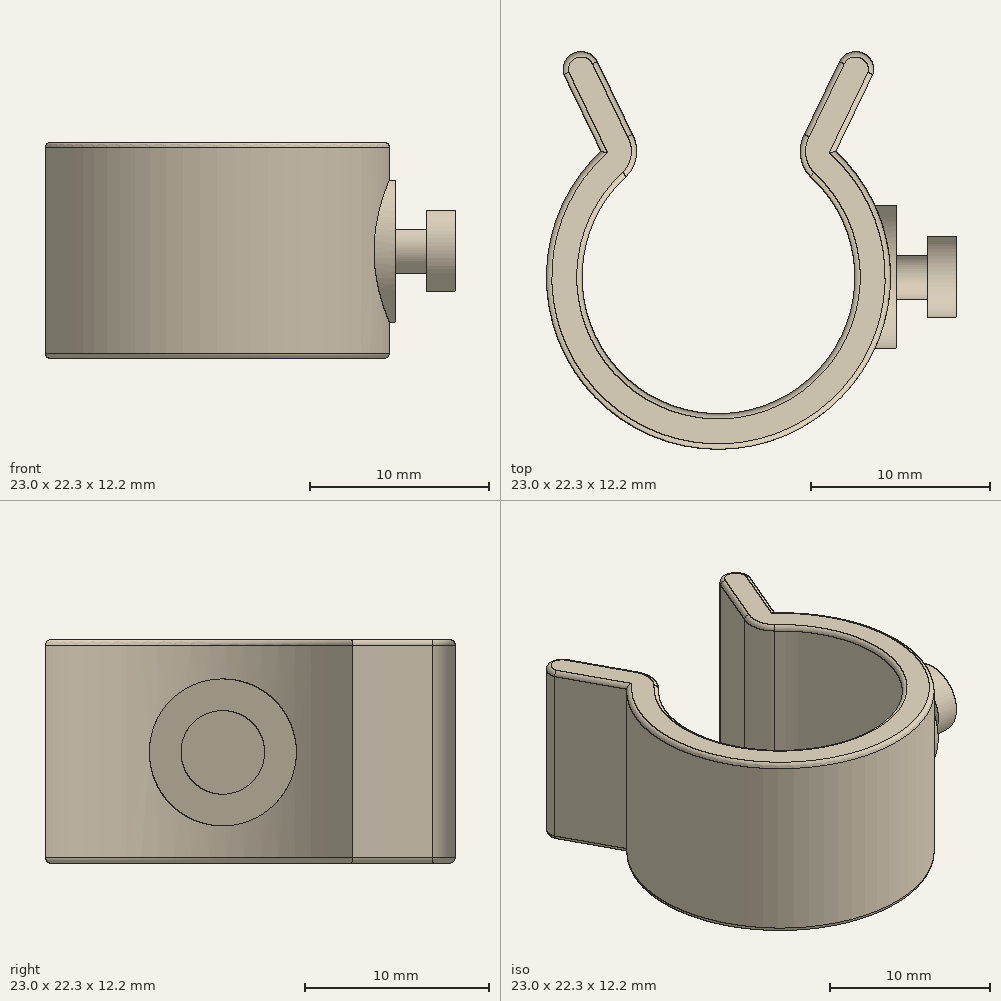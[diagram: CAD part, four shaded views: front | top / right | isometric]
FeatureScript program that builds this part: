
annotation { "Feature Type Name" : "Feature", "Feature Type Description" : "" }
export const myFeature = defineFeature(function(context is Context, id is Id, definition is map)
    precondition{}
    {
        {
            var Q0;
            Q0=qCreatedBy(makeId("Top.planeOp"),FACE);
            var sketch = newSketch(context, id + "F0", { "sketchPlane" : qUnion([Q0])});
            skArc(sketch, "E0", {"start": v(-5.16, 5.65) * mm, "mid": v(0, -7.65) * mm, "end": v(5.16, 5.65) * mm});
            skArc(sketch, "E1", {"start": v(-6.59, 7.05) * mm, "mid": v(0.01, -9.65) * mm, "end": v(6.57, 7.07) * mm});
            skLineSegment(sketch, "E2", {"start": v(7.65, 0) * mm, "end": v(9.65, 0) * mm, "construction": true});
            skArc(sketch, "E3", {"start": v(-5.16, 5.65) * mm, "mid": v(-4.6, 6.77) * mm, "end": v(-4.83, 8) * mm});
            skLineSegment(sketch, "E4", {"start": v(-6.59, 7.05) * mm, "end": v(-8.67, 11.38) * mm});
            skLineSegment(sketch, "E5", {"start": v(-4.83, 8) * mm, "end": v(-6.8, 12.09) * mm});
            skLineSegment(sketch, "E6.MirrorCS", {"start": v(4.83, 8) * mm, "end": v(6.8, 12.09) * mm});
            skLineSegment(sketch, "E7.MirrorCS", {"start": v(6.59, 7.05) * mm, "end": v(8.67, 11.38) * mm});
            skArc(sketch, "E8.MirrorCS", {"start": v(5.16, 5.65) * mm, "mid": v(4.6, 6.77) * mm, "end": v(4.83, 8) * mm});
            skLineSegment(sketch, "E9", {"start": v(-7.7, 11.65) * mm, "end": v(7.7, 11.65) * mm, "construction": true});
            skArc(sketch, "E10", {"start": v(-6.8, 12.09) * mm, "mid": v(-8.06, 12.6) * mm, "end": v(-8.67, 11.38) * mm});
            skArc(sketch, "E11.MirrorCS", {"start": v(6.8, 12.09) * mm, "mid": v(8.06, 12.6) * mm, "end": v(8.67, 11.38) * mm});
            skLineSegment(sketch, "E12", {"start": v(-4.6, 6.8) * mm, "end": v(4.6, 6.8) * mm, "construction": true});
            skSolve(sketch);
        }
        {
            var Q0;
            Q0 = qSketchRegion(id + "F0", true);
            extrude(context, id + "F1", {"entities" : qUnion([Q0]), "depth" : 12.15 * mm});
        }
        {
            var Q0;
            Q0=qCreatedBy(makeId("Right.planeOp"),FACE);
            cPlane(context, id + "F2", {"entities" : qUnion([Q0]), "cplaneType" : CPlaneType.OFFSET, "offset" : 8 * mm, "width" : 150 * mm, "height" : 150 * mm});
        }
        {
            var Q0;
            Q0=qCreatedBy(id+"F2.planeOp",FACE);
            var sketch = newSketch(context, id + "F3", { "sketchPlane" : qUnion([Q0])});
            skCircle(sketch, "E13", {"center": v(0, 6.02) * mm, "radius": 4 * mm});
            skCircle(sketch, "E14", {"center": v(0, 6.02) * mm, "radius": 1.25 * mm});
            skSolve(sketch);
        }
        {
            var Q0;
            Q0 = qSketchRegion(id + "F3", true);
            extrude(context, id + "F4", {"entities" : qUnion([Q0]), "operationType" : NewBodyOperationType.ADD, "depth" : 2 * mm});
        }
        {
            var Q0;
            Q0=makeQuery(id+"F3.imprint","IMPRINT",FACE,{"disambiguationData":[TD([[makeQuery(id+"F3.imprint","IMPRINT",EDGE,{"derivedFrom":sQuery(id+"F3.wireOp",EDGE,"E14")}),1.0]])]});
            var Q1;
            Q1=sQuery(id+"F3.wireOp",EDGE,"E14");
            extrude(context, id + "F5", {"entities" : qUnion([Q0]), "operationType" : NewBodyOperationType.ADD, "surfaceEntities" : qUnion([Q1]), "depth" : 3.75 * mm});
        }
        {
            var Q0;
            Q0=qCreatedBy(makeId("Right.planeOp"),FACE);
            cPlane(context, id + "F6", {"entities" : qUnion([Q0]), "cplaneType" : CPlaneType.OFFSET, "offset" : 11.75 * mm, "width" : 150 * mm, "height" : 150 * mm});
        }
        {
            var Q0;
            Q0=qCreatedBy(id+"F6.planeOp",FACE);
            var sketch = newSketch(context, id + "F7", { "sketchPlane" : qUnion([Q0])});
            skCircle(sketch, "E15", {"center": v(0, 6.02) * mm, "radius": 2.27 * mm});
            skSolve(sketch);
        }
        {
            var Q0;
            Q0=makeQuery(id+"F7.imprint","IMPRINT",FACE,{"disambiguationData":[TD([[makeQuery(id+"F7.imprint","IMPRINT",EDGE,{"derivedFrom":sQuery(id+"F7.wireOp",EDGE,"E15")}),1.0]])]});
            var Q1;
            Q1=sQuery(id+"F7.wireOp",EDGE,"E15");
            extrude(context, id + "F8", {"entities" : qUnion([Q0]), "operationType" : NewBodyOperationType.ADD, "surfaceEntities" : qUnion([Q1]), "depth" : 1.6 * mm});
        }
        {
            var Q0;
            Q0=makeQuery(id+"F1.opExtrude","CAP_EDGE",EDGE,{"disambiguationData":[OSD([sQuery(id+"F0.wireOp",EDGE,"E1")])],"isStart":false});
            var Q1;
            Q1=makeQuery(id+"F1.opExtrude","CAP_EDGE",EDGE,{"disambiguationData":[OSD([sQuery(id+"F0.wireOp",EDGE,"E4")])],"isStart":false});
            var Q2;
            Q2=makeQuery(id+"F1.opExtrude","CAP_EDGE",EDGE,{"disambiguationData":[OSD([sQuery(id+"F0.wireOp",EDGE,"E10")])],"isStart":false});
            var Q3;
            Q3=makeQuery(id+"F1.opExtrude","CAP_EDGE",EDGE,{"disambiguationData":[OSD([sQuery(id+"F0.wireOp",EDGE,"E5")])],"isStart":false});
            var Q4;
            Q4=makeQuery(id+"F1.opExtrude","CAP_EDGE",EDGE,{"disambiguationData":[OSD([sQuery(id+"F0.wireOp",EDGE,"E3")])],"isStart":false});
            var Q5;
            Q5=makeQuery(id+"F1.opExtrude","CAP_EDGE",EDGE,{"disambiguationData":[OSD([sQuery(id+"F0.wireOp",EDGE,"E0")])],"isStart":false});
            var Q6;
            Q6=makeQuery(id+"F1.opExtrude","CAP_EDGE",EDGE,{"disambiguationData":[OSD([sQuery(id+"F0.wireOp",EDGE,"E8.MirrorCS")])],"isStart":false});
            var Q7;
            Q7=makeQuery(id+"F1.opExtrude","CAP_EDGE",EDGE,{"disambiguationData":[OSD([sQuery(id+"F0.wireOp",EDGE,"E6.MirrorCS")])],"isStart":false});
            var Q8;
            Q8=makeQuery(id+"F1.opExtrude","CAP_EDGE",EDGE,{"disambiguationData":[OSD([sQuery(id+"F0.wireOp",EDGE,"E11.MirrorCS")])],"isStart":false});
            var Q9;
            Q9=makeQuery(id+"F1.opExtrude","CAP_EDGE",EDGE,{"disambiguationData":[OSD([sQuery(id+"F0.wireOp",EDGE,"E7.MirrorCS")])],"isStart":false});
            fillet(context, id + "F9", {"entities" : qUnion([Q0, Q1, Q2, Q3, Q4, Q5, Q6, Q7, Q8, Q9]), "radius" : 0.3 * mm, "tangentPropagation" : true, "allowEdgeOverflow" : false});
        }
        {
            var Q0;
            Q0=makeQuery(id+"F1.opExtrude","CAP_EDGE",EDGE,{"disambiguationData":[OSD([sQuery(id+"F0.wireOp",EDGE,"E7.MirrorCS")])],"isStart":true});
            var Q1;
            Q1=makeQuery(id+"F1.opExtrude","CAP_EDGE",EDGE,{"disambiguationData":[OSD([sQuery(id+"F0.wireOp",EDGE,"E11.MirrorCS")])],"isStart":true});
            var Q2;
            Q2=makeQuery(id+"F1.opExtrude","CAP_EDGE",EDGE,{"disambiguationData":[OSD([sQuery(id+"F0.wireOp",EDGE,"E6.MirrorCS")])],"isStart":true});
            var Q3;
            Q3=makeQuery(id+"F1.opExtrude","CAP_EDGE",EDGE,{"disambiguationData":[OSD([sQuery(id+"F0.wireOp",EDGE,"E8.MirrorCS")])],"isStart":true});
            var Q4;
            Q4=makeQuery(id+"F1.opExtrude","CAP_EDGE",EDGE,{"disambiguationData":[OSD([sQuery(id+"F0.wireOp",EDGE,"E0")])],"isStart":true});
            var Q5;
            Q5=makeQuery(id+"F1.opExtrude","CAP_EDGE",EDGE,{"disambiguationData":[OSD([sQuery(id+"F0.wireOp",EDGE,"E3")])],"isStart":true});
            var Q6;
            Q6=makeQuery(id+"F1.opExtrude","CAP_EDGE",EDGE,{"disambiguationData":[OSD([sQuery(id+"F0.wireOp",EDGE,"E5")])],"isStart":true});
            var Q7;
            Q7=makeQuery(id+"F1.opExtrude","CAP_EDGE",EDGE,{"disambiguationData":[OSD([sQuery(id+"F0.wireOp",EDGE,"E10")])],"isStart":true});
            var Q8;
            Q8=makeQuery(id+"F1.opExtrude","CAP_EDGE",EDGE,{"disambiguationData":[OSD([sQuery(id+"F0.wireOp",EDGE,"E4")])],"isStart":true});
            var Q9;
            Q9=makeQuery(id+"F1.opExtrude","CAP_EDGE",EDGE,{"disambiguationData":[OSD([sQuery(id+"F0.wireOp",EDGE,"E1")])],"isStart":true});
            fillet(context, id + "F10", {"entities" : qUnion([Q0, Q1, Q2, Q3, Q4, Q5, Q6, Q7, Q8, Q9]), "radius" : 0.3 * mm, "tangentPropagation" : true, "allowEdgeOverflow" : false});
        }
    });
